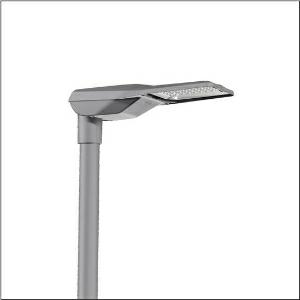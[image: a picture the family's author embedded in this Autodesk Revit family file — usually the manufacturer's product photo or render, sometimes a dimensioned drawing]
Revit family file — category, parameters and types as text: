
# Revit family: streetlight_sl_21_iq_mini___st1_0ab_5xe2m31g08jb_9670
name_source: partatom
category: Lighting Fixtures
units: mm (PartAtom-declared; Revit-internal decimal feet)

## family parameters
Cut with Voids When Loaded = No
Host = Face
Light Source = No
Part Type = Normal
Room Calculation Point = No
Round Connector Dimension = Use Diameter
Shared = No

## types (1)
- --- (1 x LED, 9530 lm, 71.6 W, 3000K)
    Apparent Load = 72 VA
    CIE Flux Codes = 40 74 97 100 100
    Color Rendering = 70
    Color Temperature = 3000K
    Default Elevation = 1800 mm
    Description = Streetlight SL 21 iQ mini, mast luminaire, primary light control with lens, of PMMA, primary optical cover: cover, of toughened safety glass, transparent, light distribution: ST1.0aB, light emission: direct distribution, primary light characteristic: asymmetric, installation type: post-top, side-entry, LED, High Power LED, rated luminous flux: 9.530lm, luminous efficacy: 133lm/W, light colour: 730, colour temperature: 3000K, control gear: iQ Street-Remote, control: Street-Remote, Auto-Match, Temp-Guard, Lumen-Switch, Night-Set, Smart-Wire, Light-Fading, Desk-Remote (wireless, voltage-free reading and setting of iQ features in the workshop via application-optimized NFC function/RFID function), optimised constant luminous flux control (CLO 2.0), pre-setting: linear dimming characteristic, mains connection: 220..240V, AC, 50/60Hz, start of lifetime: 72W, end of service life: 75W, reduction: 33W, luminaire housing, of diecast aluminium, powder-coated, Siteco® metallic grey (DB 702S), corrosivity category C5 mid according to DIN EN ISO 12944, please order mast flange separately, inclination adjustable: 0°, 5°, 10°, 15°, sealing non-destructively replaceable, multi-level sealing system, length: 628mm, width: 235mm, height: 110mm, mast flange for spigot size: 42mm (side-entry): 5XC10008XM4, 60/48mm (side-entry/post-top): 5XC10108XM2, 76/60mm (side-entry/post-top): 5XC10108XM1, mounting height: 4..8m, protection rating (complete): IP66, insulation class (complete): insulation class II (safety insulation), certification: CE, ENEC, ENEC+, VDE, impact resistance: IK10, permissible operating ambient temperature for outdoor applications: -40..+50°C, standard-compliant lighting for roads and squares, packaging unit: 1 piece

Light Distribution: ST1.0aB
    Height = 110 mm
    Lamp = 1 x LED
    Lamp Light Flux = 9530 lm
    Lamp Power = 71.6 W
    Lamp count = 1
    Length = 625 mm
    Luminous efficacy = 133 lm/W
    Manufacturer = Siteco
    ModVariant = No
    Model = 5XE2M31G08JB
    Number of Poles = 1
    OnlyDefault = Yes
    Power Factor = 1
    Product Name = Streetlight SL 21 iQ mini | ST1.0aB
    Product group = mast luminaire | pylon top
    ProductGroupID = 6100
    Protection Class = Protection class II
    Protection Degree = IP 66
    RLX_Detail_Level = 1
    RLX_Emergency_Light_Flux = 0 lm
    RLX_Emergency_Type = 0
    RLX_Emergency_Type_DB = No
    RlxData = <blob elided: 26313 chars, md5=30b2f642>
    Socket = socket
    Standby Power = 0 W
    System Light Flux = 9530 lm
    System Power = 72 W
    Type Comments = factory setting: luminous flux: 100 % | dim-lin: 254 | 746 mA
    Type Image = l_1003519.jpg
    URL = http://relux.com
    VarID = @adj_189805
    Voltage = 0 V
    Weight = 0.00 kg
    Width = 234 mm

## geometry (parser evidence)
native form markers: Blend x4, Sweep x10
no freeform markers — native parametric forms only
